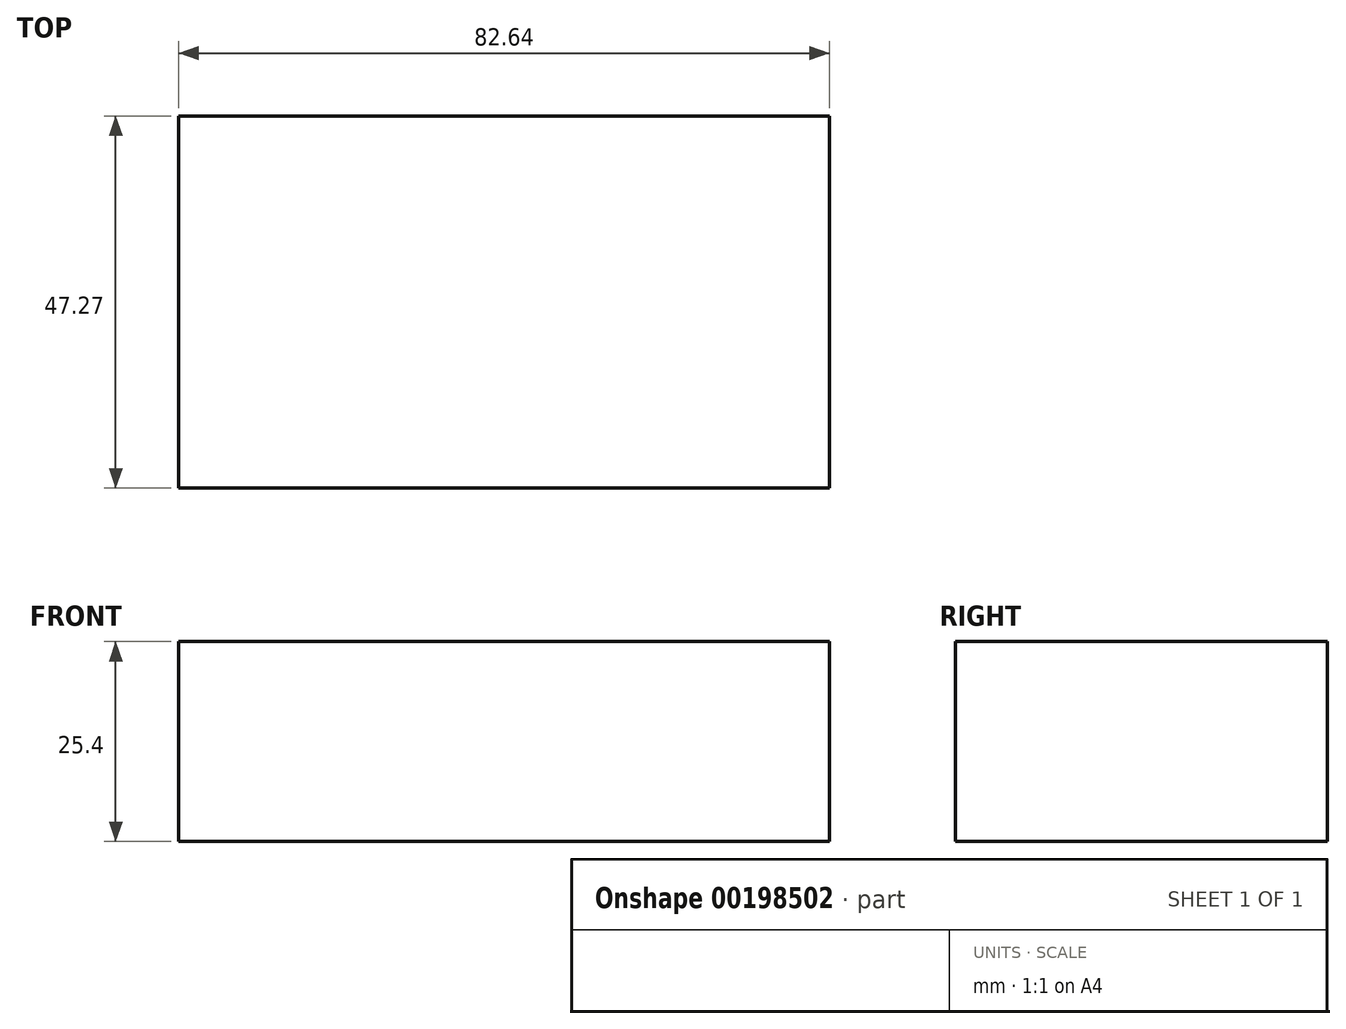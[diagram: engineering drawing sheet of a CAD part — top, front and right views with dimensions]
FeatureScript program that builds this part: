
annotation { "Feature Type Name" : "Feature", "Feature Type Description" : "" }
export const myFeature = defineFeature(function(context is Context, id is Id, definition is map)
    precondition{}
    {
        {
            var Q0;
            Q0=qCreatedBy(makeId("Top.planeOp"),FACE);
            var sketch = newSketch(context, id + "F0", { "sketchPlane" : qUnion([Q0])});
            skLineSegment(sketch, "E0.bottom", {"start": v(-31.94, 29.05) * mm, "end": v(50.7, 29.05) * mm});
            skLineSegment(sketch, "E0.top", {"start": v(-31.94, -18.22) * mm, "end": v(50.7, -18.22) * mm});
            skLineSegment(sketch, "E0.left", {"start": v(-31.94, 29.05) * mm, "end": v(-31.94, -18.22) * mm});
            skLineSegment(sketch, "E0.right", {"start": v(50.7, 29.05) * mm, "end": v(50.7, -18.22) * mm});
            skSolve(sketch);
        }
        {
            var Q0;
            Q0 = qSketchRegion(id + "F0", true);
            extrude(context, id + "F1", {"entities" : qUnion([Q0]), "depth" : 25.4 * mm});
        }
    });
